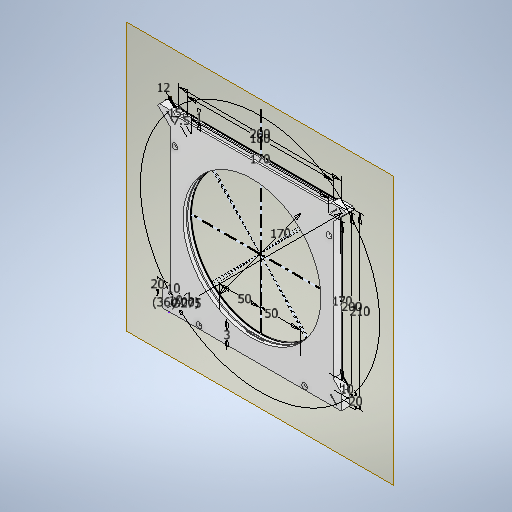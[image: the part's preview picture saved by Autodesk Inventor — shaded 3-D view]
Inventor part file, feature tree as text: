
AUTODESK INVENTOR PART (.ipt)
format: ipt  version: 2025.1 (Build 291241000, 241)  size: 849,920 bytes
history: native  units: mm
features: chamfer x6, extrude x5, sketch x3, other x3, plane x1, hole x1
ambient origin geometry x8: Origin, YZ Plane, XZ Plane, XY Plane, X Axis, Y Axis, Z Axis, Center Point
bodies: Solid1 (feature_tree)
feature tree (19):
  plane  "Work Plane1"
  sketch  "Sketch1"  dims[d0=180.0mm d1=200.0mm]
  extrude  "Extrusion1"  Depth=200.0mm
  extrude  "Extrusion2"  Depth=210.0mm
  extrude  "Extrusion3"  Depth=170.0mm
  chamfer  "Chamfer3"  Distance=50.0mm
  chamfer  "Chamfer4"  Distance=50.0mm
  chamfer  "Chamfer5"  Distance=10.0mm
  chamfer  "Chamfer6"  Distance=4.25mm
  hole  "Hole1"  [1 undecoded]
  extrude  "Extrusion4"  Depth=10.0mm TaperAngle=45.0deg
  extrude  "Extrusion5"  Depth=10.0mm TaperAngle=45.0deg
  chamfer  "Chamfer7"  Distance=0.5mm Angle=45.0deg
  chamfer  "Chamfer8"  Distance=3.0mm Angle=45.0deg
  sketch  "Sketch2"  dims[d4=170.0mm d5=170.0mm d6=50.0mm d7=50.0mm d8=10.0mm d9=0.0mm d10=4.25mm d11=0.0mm d12=4.25mm d13=0.0mm d20=10.0mm d21=1.5mm d22=45.0deg d23=10.0mm d24=1.5mm d25=45.0deg d26=2.0mm d27=0.5mm d28=45.0deg d29=3.0mm d30=1.0mm d31=45.0deg d32=20.0mm d33=10.0mm d34=3.0mm d35=10.0mm d36=20.0mm d38=12.0mm d40=1.0mm d41=35.0mm d42=35.0mm d43=5.0mm d44=180.0mm d45=5.0mm d46=3.797mm d47=6.0mm d48=7.087mm d49=2.0mm d50=14.3117mm d51=8.0mm d52=20.594885mm d53=170.0mm d54=2.0mm d55=0.0mm d56=10.0mm d57=0.0mm d58=2.0mm d59=6.0mm d60=45.0deg d61=2.0mm d62=6.0mm d63=45.0deg d65=10.0mm d66=40.0mm d68=360.0deg d70=275.0mm d71=4.0mm d72=1.0mm d73=15.0mm d74=7.5mm]
  sketch  "Sketch Circular Pattern1"  dims[d2=200.0mm d3=210.0mm]
  parser-record x1  (decoder bookkeeping rows leaked as tree rows — omitted from the tree; the rows remain in map.json)
  other  "Target Holder With Sensors.iam"
  other  "Front Plate:1"
note: 1 required parameter value undecoded (feature->parameter linkage not recoverable at this tier; creation-order binding heuristic only, values carry confidence <= 0.55)
note: 1 file-system path scrubbed to <path> (originals preserved in map.json)
